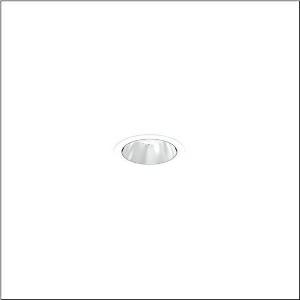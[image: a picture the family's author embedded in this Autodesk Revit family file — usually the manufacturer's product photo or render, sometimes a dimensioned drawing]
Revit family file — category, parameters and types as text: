
# Revit family: lunis_21_s_51db15ma91c
name_source: partatom
category: Lighting Fixtures
units: mm (PartAtom-declared; Revit-internal decimal feet)

## family parameters
Cut with Voids When Loaded = No
Host = Face
Light Source = No
Part Type = Normal
Room Calculation Point = No
Round Connector Dimension = Use Diameter
Shared = No

## types (1)
- --- (1 x LED, 980 lm, 5.9 W, 6500K)
    Apparent Load = 6 VA
    CIE Flux Codes = 93 99 100 100 100
    Color Rendering = 80
    Color Temperature = 6500K
    Default Elevation = 1800 mm
    Description = Lunis 21 S, downlight, light control with lens, of PMMA, anti glare with reflector, of PC, highly specular, light emission: direct distribution, LED rated luminous flux: 990lm, light colour: 830/840/865, with terminal, 3-pole, mains connection: 220..240V, AC, 50..60Hz, housing, round, of diecast aluminium, traffic white (RAL 9016), diameter: 84mm, clamping range: 1..40mm, protection rating (complete): IP20, protection rating (on room side): IP54, insulation class (complete): insulation class II (safety insulation), certification: CE, impact resistance: IK03, packaging unit: 1 piece
    Height = 0 mm  [stored 0 ft]
    Lamp = 1 x LED
    Lamp Light Flux = 980 lm
    Lamp Power = 5.9 W
    Lamp count = 1
    Length = 84 mm
    Luminous efficacy = 166 lm/W
    Manufacturer = Siteco
    ModVariant = No
    Model = 51DB15MA91C
    Mounting Place = Ceiling
    Mounting Type = Recessed
    Number of Poles = 1
    OnlyDefault = Yes
    Power Factor = 1
    Product Name = Lunis 21 S
    Product group = downlight
    ProductGroupID = 401
    Protection Class = Protection class II
    Protection Degree = IP 20
    RLX_Detail_Level = 1
    RLX_Emergency_Light_Flux = 0 lm
    RLX_Emergency_Type = 0
    RLX_Emergency_Type_DB = No
    RlxData = <blob elided: 8353 chars, md5=f14b6e17>
    Socket = socket
    Standby Power = 0 W
    System Light Flux = 980 lm
    System Power = 6 W
    Type Comments = individual setting: colour temperature 6500K
    Type Image = l_1290840.jpg
    URL = http://relux.com
    VarID = @adj_036605
    Voltage = 0 V
    Weight = 0.00 kg
    Width = 0 mm  [stored 0 ft]

note: [stored X ft] marks values corroborated as IEEE doubles in the binary element streams (Revit-internal decimal feet)

## geometry (parser evidence)
native form markers: Sweep x8
no freeform markers — native parametric forms only
